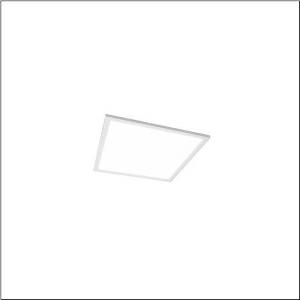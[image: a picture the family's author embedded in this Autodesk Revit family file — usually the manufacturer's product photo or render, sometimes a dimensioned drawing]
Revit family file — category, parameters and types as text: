
# Revit family: apollon_21_square_51mq13wd2414
name_source: partatom
category: Lighting Fixtures
units: mm (PartAtom-declared; Revit-internal decimal feet)

## family parameters
Cut with Voids When Loaded = No
Host = Face
Light Source = No
Part Type = Normal
Room Calculation Point = No
Round Connector Dimension = Use Diameter
Shared = No

## types (1)
- Apollon 21 square (1 x LED, 1800 lm, 14 W, 4000K)
    Apparent Load = 14 VA
    CIE Flux Codes = 68 89 97 100 100
    Color Rendering = 80
    Color Temperature = 4000K
    Default Elevation = 1800 mm  [stored 5.90551 ft]
    Description = Apollon 21 square, office luminaire, primary optical cover: micro prismatic cover, of PMMA, CAT 2 (L<= 3000cd/m²), light emission: direct distribution, primary light characteristic: symmetric, installation type: recessed, LED, rated luminous flux: 1.800lm, luminous efficacy: 129lm/W, light colour: 840, colour temperature: 4000K, control gear: DALI 2, with terminal, 5-pole, mains connection: 220..240V, AC/DC, 0/50..60Hz, rated input power: 14W, suitable for self-contained emergency lighting element 59MQE002602A with integrated self-test function according to EN 60598-2-22, housing, of sheet steel, coated, traffic white (RAL 9016), length: 296mm, width: 296mm, height: 55mm, recess depth: 180mm, housing upper side, of sheet steel, galvanised, protection rating (complete): IP20, protection rating (lamp compartment, on room side): IP50, insulation class (complete): insulation class II (safety insulation), certification: CE, ENEC, impact resistance: IK03, permissible operating ambient temperature: -20..+45°C, permissible storage temperature: -40..+80°C, standard: EN 60598-2-22, packaging unit: 1 piece
    Height = 0 mm  [stored 0 ft]
    Lamp = 1 x LED
    Lamp Light Flux = 1800 lm
    Lamp Power = 14 W
    Lamp count = 1
    Length = 295 mm
    Luminous efficacy = 129 lm/W
    Manufacturer = Siteco
    ModVariant = No
    Model = 51MQ13WD2414
    Mounting Place = Ceiling
    Mounting Type = Recessed
    Number of Poles = 1
    OnlyDefault = Yes
    Power Factor = 1
    Product Name = Apollon 21 square
    Product group = office luminaire | ceiling recessed
    ProductGroupID = 400
    Protection Class = Protection class II
    Protection Degree = IP 20
    RLX_Detail_Level = 1
    RLX_Emergency_Light_Flux = 0 lm
    RLX_Emergency_Type = 0
    RLX_Emergency_Type_DB = No
    RlxData = <blob elided: 9449 chars, md5=5662fc5c>
    Socket = socket
    Standby Power = 0 W
    System Light Flux = 1800 lm
    System Power = 14 W
    Type Comments = Product without accessories
    Type Image = l_1291030.jpg
    URL = http://relux.com
    VarID = ---
    Voltage = 0 V
    Weight = 0.00 kg
    Width = 295 mm

note: [stored X ft] marks values corroborated as IEEE doubles in the binary element streams (Revit-internal decimal feet)

## geometry (parser evidence)
native form markers: Sweep x8
no freeform markers — native parametric forms only
